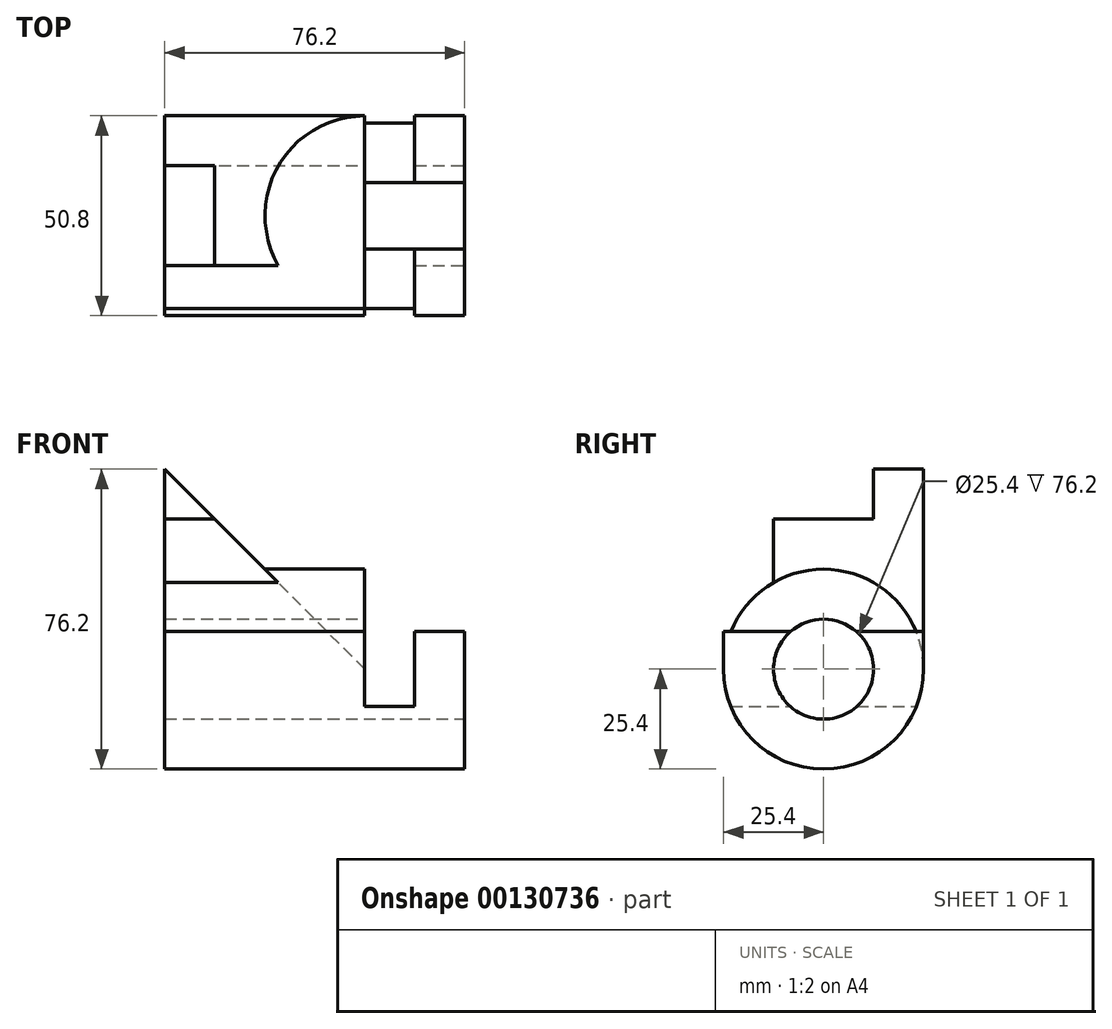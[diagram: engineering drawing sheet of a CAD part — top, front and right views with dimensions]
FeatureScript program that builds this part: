
annotation { "Feature Type Name" : "Feature", "Feature Type Description" : "" }
export const myFeature = defineFeature(function(context is Context, id is Id, definition is map)
    precondition{}
    {
        {
            var Q0;
            Q0=qCreatedBy(makeId("Front.planeOp"),FACE);
            var sketch = newSketch(context, id + "F0", { "sketchPlane" : qUnion([Q0])});
            skLineSegment(sketch, "E0.bottom", {"start": v(0, 0) * mm, "end": v(76.2, 0) * mm});
            skLineSegment(sketch, "E0.top", {"start": v(0, 76.2) * mm, "end": v(76.2, 76.2) * mm});
            skLineSegment(sketch, "E0.left", {"start": v(0, 0) * mm, "end": v(0, 76.2) * mm});
            skLineSegment(sketch, "E0.right", {"start": v(76.2, 0) * mm, "end": v(76.2, 76.2) * mm});
            skLineSegment(sketch, "E1", {"start": v(0, 76.2) * mm, "end": v(28.58, 47.63) * mm});
            skLineSegment(sketch, "E2", {"start": v(28.57, 47.62) * mm, "end": v(0, 47.62) * mm});
            skLineSegment(sketch, "E3", {"start": v(28.57, 47.63) * mm, "end": v(47.58, 28.62) * mm, "construction": true});
            skLineSegment(sketch, "E4", {"start": v(47.58, 28.62) * mm, "end": v(0, 28.62) * mm, "construction": true});
            skLineSegment(sketch, "E5", {"start": v(25.4, 50.8) * mm, "end": v(50.8, 50.8) * mm});
            skLineSegment(sketch, "E6", {"start": v(50.8, 50.8) * mm, "end": v(50.8, 15.87) * mm});
            skLineSegment(sketch, "E7", {"start": v(50.8, 15.87) * mm, "end": v(63.5, 15.87) * mm});
            skLineSegment(sketch, "E8", {"start": v(63.5, 15.87) * mm, "end": v(63.5, 34.92) * mm});
            skLineSegment(sketch, "E9", {"start": v(63.5, 34.92) * mm, "end": v(76.2, 34.92) * mm});
            skLineSegment(sketch, "E10", {"start": v(0, 63.5) * mm, "end": v(12.7, 63.5) * mm});
            skSolve(sketch);
        }
        {
            var Q0;
            {var subQ4=sQuery(id+"F0.wireOp",EDGE,"E0.bottom");Q0=makeQuery(id+"F0.imprint","IMPRINT",FACE,{"disambiguationData":[TD([[makeQuery(id+"F0.imprint","IMPRINT",EDGE,{"derivedFrom":subQ4}),1.0]])]});}
            var Q1;
            {var subQ3=sQuery(id+"F0.wireOp",EDGE,"E10");Q1=makeQuery(id+"F0.imprint","IMPRINT",FACE,{"disambiguationData":[TD([[makeQuery(id+"F0.imprint","IMPRINT",EDGE,{"derivedFrom":subQ3}),1.0]])]});}
            var Q2;
            {var subQ0=sQuery(id+"F0.wireOp",EDGE,"E2");Q2=makeQuery(id+"F0.imprint","IMPRINT",FACE,{"disambiguationData":[TD([[makeQuery(id+"F0.imprint","IMPRINT",EDGE,{"derivedFrom":subQ0}),-1.0]])]});}
            extrude(context, id + "F1", {"entities" : qUnion([Q0, Q1, Q2]), "depth" : 50.8 * mm});
        }
        {
            var Q0;
            Q0=makeQuery(id+"F1.opExtrude","SWEPT_FACE",FACE,{"disambiguationData":[OSD([sQuery(id+"F0.wireOp",EDGE,"E0.right")])]});
            var sketch = newSketch(context, id + "F2", { "sketchPlane" : qUnion([Q0])});
            skLineSegment(sketch, "E11", {"start": v(-12.7, 63.5) * mm, "end": v(-12.7, 76.2) * mm});
            skLineSegment(sketch, "E12", {"start": v(0, 76.2) * mm, "end": v(-12.7, 76.2) * mm});
            skCircle(sketch, "E13", {"center": v(-25.4, 25.4) * mm, "radius": 25.4 * mm});
            skCircle(sketch, "E14", {"center": v(-25.4, 25.4) * mm, "radius": 12.7 * mm});
            skLineSegment(sketch, "E15", {"start": v(-12.7, 63.5) * mm, "end": v(-38.1, 63.5) * mm});
            skLineSegment(sketch, "E16", {"start": v(-38.1, 63.5) * mm, "end": v(-38.1, 47.4) * mm});
            skLineSegment(sketch, "E17", {"start": v(0, 76.2) * mm, "end": v(0, 25.4) * mm});
            skLineSegment(sketch, "E18", {"start": v(-12.7, 76.2) * mm, "end": v(-50.8, 76.2) * mm});
            skLineSegment(sketch, "E19", {"start": v(-50.8, 76.2) * mm, "end": v(-50.8, 25.4) * mm});
            skArc(sketch, "E20", {"start": v(-38.1, 47.4) * mm, "mid": v(-47.4, 38.1) * mm, "end": v(-50.8, 25.4) * mm});
            skSolve(sketch);
        }
        {
            var Q0;
            {var subQ0=sQuery(id+"F2.wireOp",EDGE,"E13");var subQ1=sQuery(id+"F0.wireOp",EDGE,"E0.right");var subQ2=makeQuery(id+"F1.opExtrude","CAP_EDGE",EDGE,{"disambiguationData":[OSD([subQ1])],"isStart":false});var subQ3=makeQuery(id+"F2.imprint","INTERSECT",VERTEX,{"derivedFrom":[subQ2,subQ0]});Q0=makeQuery(id+"F2.imprint","IMPRINT",FACE,{"disambiguationData":[TD([[makeQuery(id+"F2.imprint","IMPRINT",EDGE,{"disambiguationData":[TD([[subQ3,-1.0]])],"derivedFrom":subQ0}),-1.0]])]});}
            var Q1;
            {var subQ0=sQuery(id+"F2.wireOp",EDGE,"E13");var subQ1=sQuery(id+"F0.wireOp",EDGE,"E0.right");var subQ2=makeQuery(id+"F1.opExtrude","CAP_EDGE",EDGE,{"disambiguationData":[OSD([subQ1])],"isStart":true});var subQ3=makeQuery(id+"F2.imprint","INTERSECT",VERTEX,{"derivedFrom":[subQ2,subQ0,sQuery(id+"F2.wireOp",EDGE,"E17")]});Q1=makeQuery(id+"F2.imprint","IMPRINT",FACE,{"disambiguationData":[TD([[makeQuery(id+"F2.imprint","IMPRINT",EDGE,{"disambiguationData":[TD([[subQ3,1.0]])],"derivedFrom":subQ0}),-1.0]])]});}
            var Q2;
            {var subQ0=sQuery(id+"F2.wireOp",EDGE,"E19");var subQ1=sQuery(id+"F2.wireOp",EDGE,"E13");var subQ2=sQuery(id+"F0.wireOp",EDGE,"E0.right");var subQ3=makeQuery(id+"F2.imprint","INTERSECT",VERTEX,{"derivedFrom":[makeQuery(id+"F1.opExtrude","CAP_EDGE",EDGE,{"disambiguationData":[OSD([subQ2])],"isStart":false}),subQ1,subQ0]});Q2=makeQuery(id+"F2.imprint","IMPRINT",FACE,{"disambiguationData":[TD([[makeQuery(id+"F2.imprint","IMPRINT",EDGE,{"disambiguationData":[TD([[subQ3,1.0]])],"derivedFrom":subQ1}),-1.0]])]});}
            var Q3;
            Q3=makeQuery(id+"F2.imprint","IMPRINT",FACE,{"disambiguationData":[TD([[makeQuery(id+"F2.imprint","IMPRINT",EDGE,{"derivedFrom":sQuery(id+"F2.wireOp",EDGE,"E11")}),1.0]])]});
            var Q4;
            {var subQ0=sQuery(id+"F2.wireOp",EDGE,"E14");var subQ1=makeQuery(id+"F1.opExtrude","SWEPT_EDGE",EDGE,{"disambiguationData":[OSD([sQuery(id+"F0.wireOp",EDGE,"E0.right"),sQuery(id+"F0.wireOp",EDGE,"E9")])]});var subQ2=makeQuery(id+"F2.imprint","INTERSECT",VERTEX,{"disambiguationData":[OD(0.0)],"derivedFrom":[subQ1,subQ0]});Q4=makeQuery(id+"F2.imprint","IMPRINT",FACE,{"disambiguationData":[TD([[makeQuery(id+"F2.imprint","IMPRINT",EDGE,{"disambiguationData":[TD([[subQ2,1.0]])],"derivedFrom":subQ0}),1.0]])]});}
            var Q5;
            {var subQ0=sQuery(id+"F2.wireOp",EDGE,"E14");var subQ1=makeQuery(id+"F1.opExtrude","SWEPT_EDGE",EDGE,{"disambiguationData":[OSD([sQuery(id+"F0.wireOp",EDGE,"E0.right"),sQuery(id+"F0.wireOp",EDGE,"E9")])]});var subQ2=makeQuery(id+"F2.imprint","INTERSECT",VERTEX,{"disambiguationData":[OD(0.0)],"derivedFrom":[subQ1,subQ0]});Q5=makeQuery(id+"F2.imprint","IMPRINT",FACE,{"disambiguationData":[TD([[makeQuery(id+"F2.imprint","IMPRINT",EDGE,{"disambiguationData":[TD([[subQ2,-1.0]])],"derivedFrom":subQ0}),1.0]])]});}
            extrude(context, id + "F3", {"entities" : qUnion([Q0, Q1, Q2, Q3, Q4, Q5]), "operationType" : NewBodyOperationType.REMOVE, "endBound" : BoundingType.THROUGH_ALL, "oppositeDirection" : true, "depth" : 25.4 * mm});
        }
        {
            var Q0;
            Q0=makeQuery(id+"F1.opExtrude","SWEPT_FACE",FACE,{"disambiguationData":[OSD([sQuery(id+"F0.wireOp",EDGE,"E6")])]});
            var sketch = newSketch(context, id + "F4", { "sketchPlane" : qUnion([Q0])});
            skLineSegment(sketch, "E21", {"start": v(-38.1, 50.8) * mm, "end": v(0, 50.8) * mm});
            skLineSegment(sketch, "E22", {"start": v(0, 50.8) * mm, "end": v(0, 25.4) * mm});
            skLineSegment(sketch, "E23", {"start": v(-38.1, 50.8) * mm, "end": v(-38.1, 47.4) * mm});
            skArc(sketch, "E24", {"start": v(0, 25.4) * mm, "mid": v(-12.7, 47.4) * mm, "end": v(-38.1, 47.4) * mm});
            skSolve(sketch);
        }
        {
            var Q0;
            {var subQ0=sQuery(id+"F4.wireOp",EDGE,"E23");Q0=makeQuery(id+"F4.imprint","IMPRINT",FACE,{"disambiguationData":[TD([[makeQuery(id+"F4.imprint","IMPRINT",EDGE,{"derivedFrom":subQ0}),1.0]])]});}
            var Q1;
            Q1=makeQuery(id+"F1.opExtrude","SWEPT_FACE",FACE,{"disambiguationData":[OSD([sQuery(id+"F0.wireOp",EDGE,"E1")])]});
            extrude(context, id + "F5", {"entities" : qUnion([Q0]), "operationType" : NewBodyOperationType.REMOVE, "endBound" : BoundingType.UP_TO_SURFACE, "oppositeDirection" : true, "endBoundEntityFace" : qUnion([Q1]), "depth" : 25.4 * mm});
        }
        {
            var Q0;
            {var subQ0=sQuery(id+"F4.wireOp",EDGE,"E22");Q0=makeQuery(id+"F4.imprint","IMPRINT",FACE,{"disambiguationData":[TD([[makeQuery(id+"F4.imprint","IMPRINT",EDGE,{"derivedFrom":subQ0}),-1.0]])]});}
            var Q1;
            {var subQ0=sQuery(id+"F0.wireOp",EDGE,"E1");Q1=makeQuery(id+"F5.boolean.opBoolean","MERGE",FACE,{"derivedFrom":[makeQuery(id+"F1.opExtrude","SWEPT_FACE",FACE,{"disambiguationData":[OSD([subQ0])]}),makeQuery(id+"F5.opExtrude","CAP_FACE",FACE,{"disambiguationData":[OSD([subQ0])],"isStart":false})]});}
            extrude(context, id + "F6", {"entities" : qUnion([Q0]), "operationType" : NewBodyOperationType.REMOVE, "endBound" : BoundingType.UP_TO_SURFACE, "oppositeDirection" : true, "endBoundEntityFace" : qUnion([Q1]), "depth" : 25.4 * mm});
        }
    });
